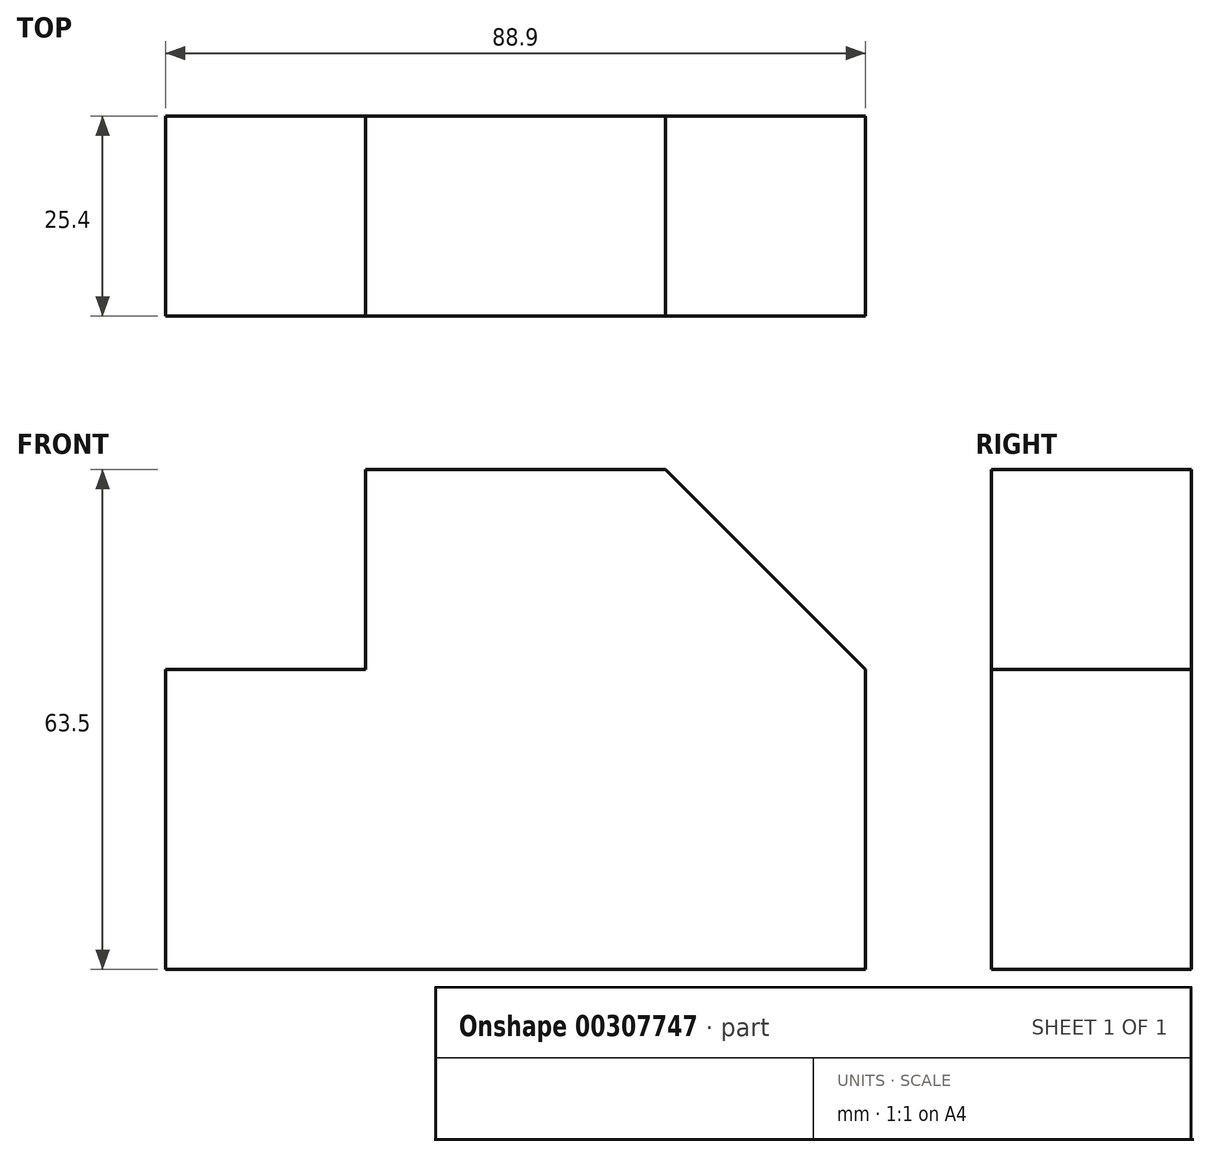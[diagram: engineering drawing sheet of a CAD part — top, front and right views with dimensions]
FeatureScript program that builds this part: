
annotation { "Feature Type Name" : "Feature", "Feature Type Description" : "" }
export const myFeature = defineFeature(function(context is Context, id is Id, definition is map)
    precondition{}
    {
        {
            var Q0;
            Q0=qCreatedBy(makeId("Front.planeOp"),FACE);
            var sketch = newSketch(context, id + "F0", { "sketchPlane" : qUnion([Q0])});
            skLineSegment(sketch, "E0", {"start": v(-55.9, -55.25) * mm, "end": v(33, -55.25) * mm});
            skLineSegment(sketch, "E1", {"start": v(33, -55.25) * mm, "end": v(33, -17.15) * mm});
            skLineSegment(sketch, "E2", {"start": v(-55.9, -55.25) * mm, "end": v(-55.9, -17.15) * mm});
            skLineSegment(sketch, "E3", {"start": v(-55.9, -17.15) * mm, "end": v(-30.5, -17.15) * mm});
            skLineSegment(sketch, "E4", {"start": v(-30.5, -17.15) * mm, "end": v(-30.5, 8.25) * mm});
            skLineSegment(sketch, "E5", {"start": v(-30.5, 8.25) * mm, "end": v(7.6, 8.25) * mm});
            skLineSegment(sketch, "E6", {"start": v(7.6, 8.25) * mm, "end": v(33, -17.15) * mm});
            skSolve(sketch);
        }
        {
            var Q0;
            Q0=makeQuery(id+"F0.imprint","IMPRINT",FACE,{"disambiguationData":[TD([[makeQuery(id+"F0.imprint","IMPRINT",EDGE,{"derivedFrom":sQuery(id+"F0.wireOp",EDGE,"E0")}),1.0]])]});
            extrude(context, id + "F1", {"entities" : qUnion([Q0]), "depth" : 25.4 * mm});
        }
    });
